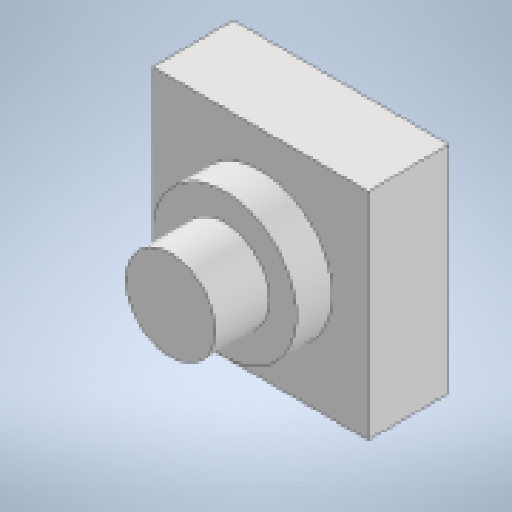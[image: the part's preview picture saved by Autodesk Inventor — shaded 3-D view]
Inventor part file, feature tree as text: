
AUTODESK INVENTOR PART (.ipt)
format: ipt  version: 2025.2 (Build 292293000, 293)  size: 136,192 bytes
history: native  units: mm
features: extrude x3, sketch x3, other x1
ambient origin geometry x8: Origin, YZ Plane, XZ Plane, XY Plane, X Axis, Y Axis, Z Axis, Center Point
bodies: Body1 (feature_tree)
feature tree (7):
  other  "ソリッド1"
  extrude  "押し出し1"  Depth=12.0mm
  extrude  "押し出し2"  Depth=12.0mm
  extrude  "押し出し3"  Depth=4.5mm TaperAngle=0.0deg
  sketch  "スケッチ1"
  sketch  "スケッチ2"
  sketch  "スケッチ3"
